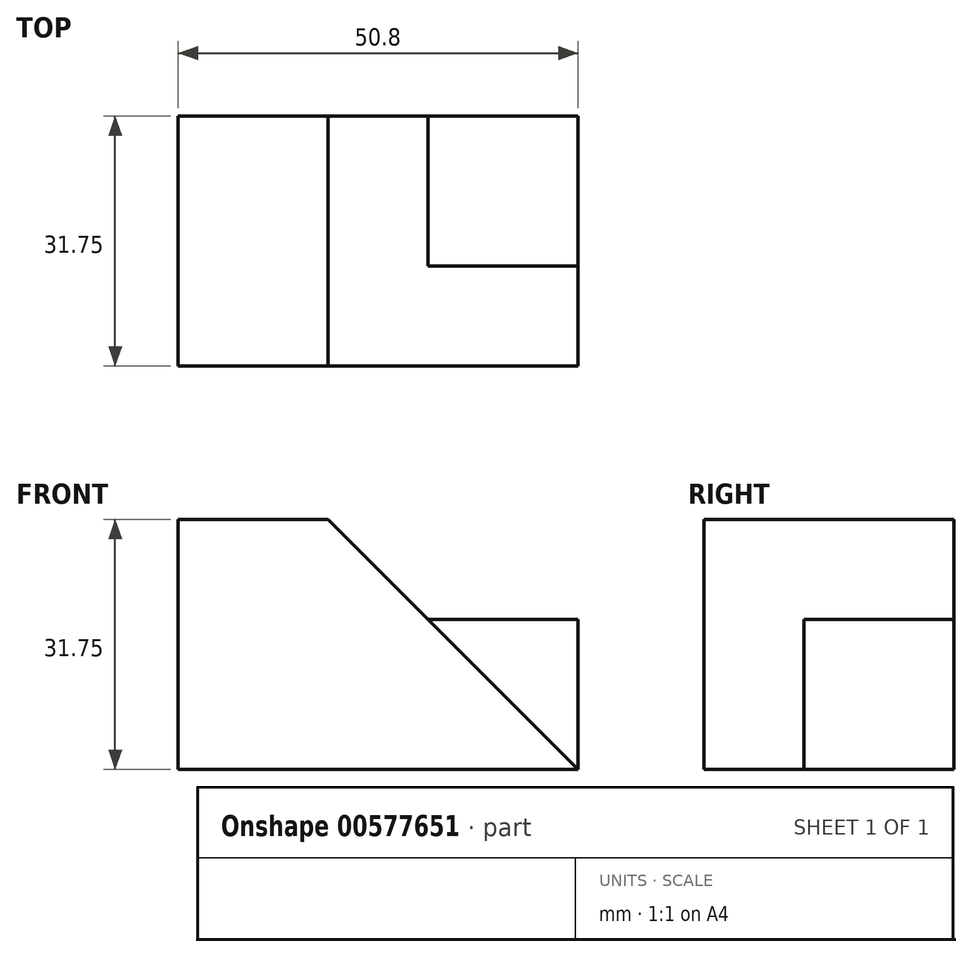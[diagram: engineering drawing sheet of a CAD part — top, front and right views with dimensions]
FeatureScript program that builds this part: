
annotation { "Feature Type Name" : "Feature", "Feature Type Description" : "" }
export const myFeature = defineFeature(function(context is Context, id is Id, definition is map)
    precondition{}
    {
        {
            var Q0;
            Q0=qCreatedBy(makeId("Front.planeOp"),FACE);
            var sketch = newSketch(context, id + "F0", { "sketchPlane" : qUnion([Q0])});
            skLineSegment(sketch, "E0", {"start": v(-64, 0) * mm, "end": v(-13.2, 0) * mm});
            skLineSegment(sketch, "E1", {"start": v(-13.2, 0) * mm, "end": v(-13.2, 31.75) * mm});
            skLineSegment(sketch, "E2", {"start": v(-13.2, 31.75) * mm, "end": v(-64, 31.75) * mm});
            skLineSegment(sketch, "E3", {"start": v(-64, 31.75) * mm, "end": v(-64, 0) * mm});
            skSolve(sketch);
        }
        {
            var Q0;
            Q0=makeQuery(id+"F0.imprint","IMPRINT",FACE,{"disambiguationData":[TD([[makeQuery(id+"F0.imprint","IMPRINT",EDGE,{"derivedFrom":sQuery(id+"F0.wireOp",EDGE,"E0")}),1.0]])]});
            extrude(context, id + "F1", {"entities" : qUnion([Q0]), "depth" : 31.75 * mm, "offsetDistance" : 25.4 * mm});
        }
        {
            var Q0;
            Q0=makeQuery(id+"F1.opExtrude","CAP_FACE",FACE,{"disambiguationData":[OSD([sQuery(id+"F0.wireOp",EDGE,"E0"),sQuery(id+"F0.wireOp",EDGE,"E1"),sQuery(id+"F0.wireOp",EDGE,"E2"),sQuery(id+"F0.wireOp",EDGE,"E3")])],"isStart":false});
            var sketch = newSketch(context, id + "F2", { "sketchPlane" : qUnion([Q0])});
            skLineSegment(sketch, "E4", {"start": v(-64, 31.75) * mm, "end": v(-44.94, 31.75) * mm});
            skLineSegment(sketch, "E5", {"start": v(-13.2, 0) * mm, "end": v(-13.2, 19.05) * mm});
            skLineSegment(sketch, "E6", {"start": v(-13.2, 19.05) * mm, "end": v(-32.24, 19.05) * mm});
            skLineSegment(sketch, "E7", {"start": v(-32.24, 19.05) * mm, "end": v(-44.94, 31.75) * mm});
            skSolve(sketch);
        }
        {
            var Q0;
            {var subQ0=sQuery(id+"F2.wireOp",EDGE,"E6");Q0=makeQuery(id+"F2.imprint","IMPRINT",FACE,{"disambiguationData":[TD([[makeQuery(id+"F2.imprint","IMPRINT",EDGE,{"derivedFrom":subQ0}),-1.0]])]});}
            extrude(context, id + "F3", {"entities" : qUnion([Q0]), "operationType" : NewBodyOperationType.REMOVE, "oppositeDirection" : true, "depth" : 31.75 * mm, "offsetDistance" : 25.4 * mm});
        }
        {
            var Q0;
            Q0=makeQuery(id+"F1.opExtrude","CAP_FACE",FACE,{"disambiguationData":[OSD([sQuery(id+"F0.wireOp",EDGE,"E0"),sQuery(id+"F0.wireOp",EDGE,"E1"),sQuery(id+"F0.wireOp",EDGE,"E2"),sQuery(id+"F0.wireOp",EDGE,"E3")])],"isStart":false});
            var sketch = newSketch(context, id + "F4", { "sketchPlane" : qUnion([Q0])});
            skLineSegment(sketch, "E8", {"start": v(-32.24, 19.05) * mm, "end": v(-13.2, 0) * mm});
            skLineSegment(sketch, "E9", {"start": v(-13.2, 0) * mm, "end": v(-13.2, 19.05) * mm});
            skLineSegment(sketch, "E10", {"start": v(-13.2, 19.05) * mm, "end": v(-32.24, 19.05) * mm});
            skSolve(sketch);
        }
        {
            var Q0;
            Q0=makeQuery(id+"F4.imprint","IMPRINT",FACE,{"disambiguationData":[TD([[makeQuery(id+"F4.imprint","IMPRINT",EDGE,{"derivedFrom":sQuery(id+"F4.wireOp",EDGE,"E8")}),1.0]])]});
            extrude(context, id + "F5", {"entities" : qUnion([Q0]), "operationType" : NewBodyOperationType.REMOVE, "oppositeDirection" : true, "depth" : 12.7 * mm, "offsetDistance" : 25.4 * mm});
        }
    });
